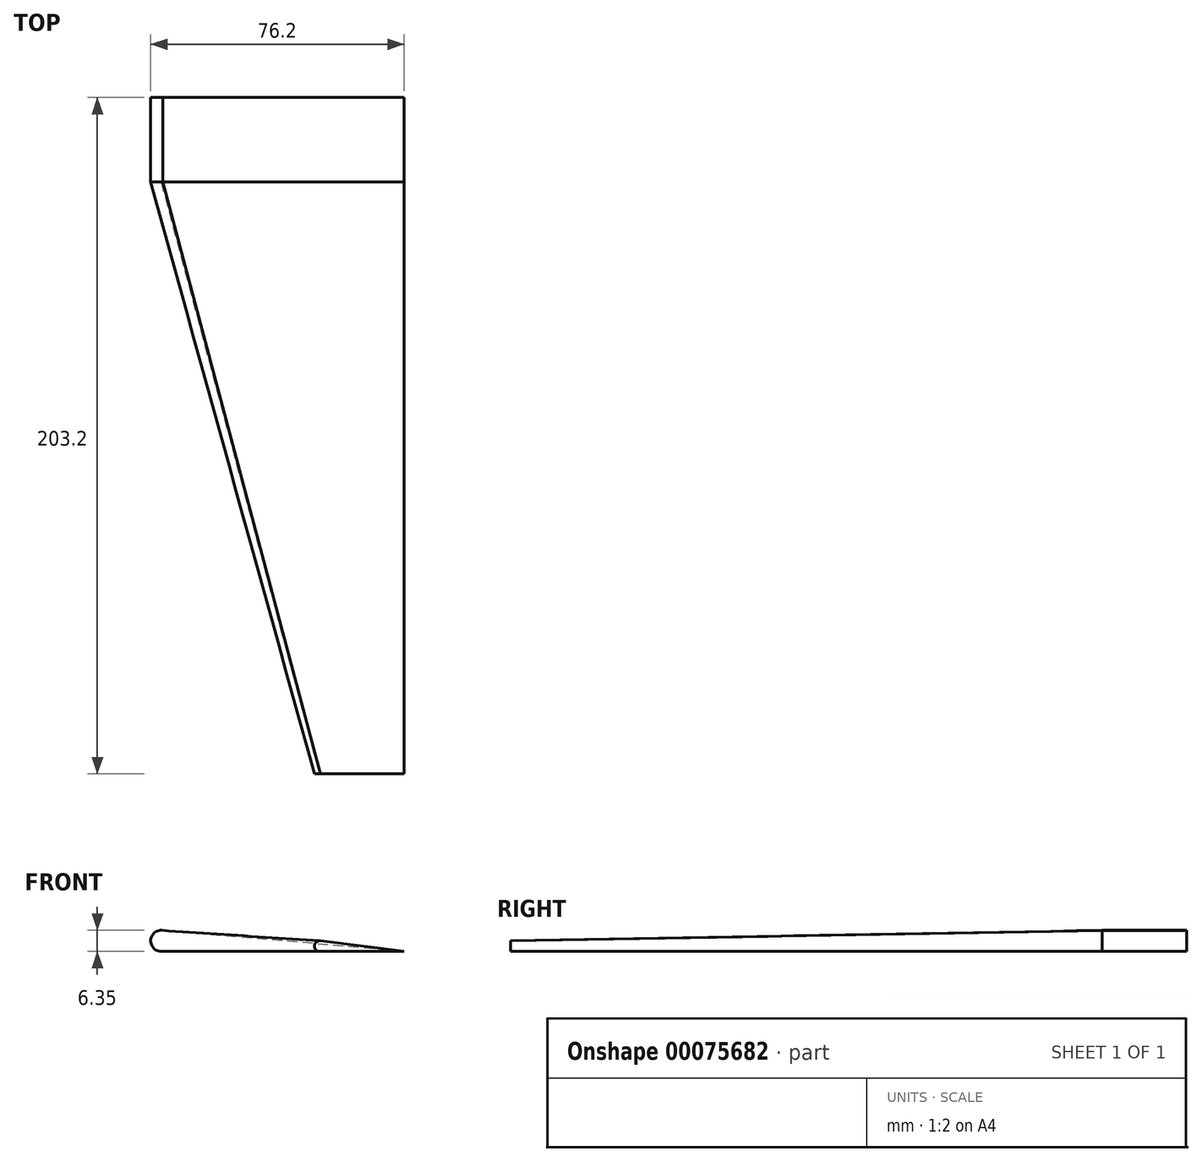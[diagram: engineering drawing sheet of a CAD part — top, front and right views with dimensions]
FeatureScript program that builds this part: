
annotation { "Feature Type Name" : "Feature", "Feature Type Description" : "" }
export const myFeature = defineFeature(function(context is Context, id is Id, definition is map)
    precondition{}
    {
        {
            var Q0;
            Q0=qCreatedBy(makeId("Front.planeOp"),FACE);
            var sketch = newSketch(context, id + "F0", { "sketchPlane" : qUnion([Q0])});
            skLineSegment(sketch, "E0", {"start": v(0, 0) * mm, "end": v(-72.58, 6.32) * mm});
            skLineSegment(sketch, "E1", {"start": v(0, 0) * mm, "end": v(-73.03, 0) * mm});
            skArc(sketch, "E2", {"start": v(-72.58, 6.32) * mm, "mid": v(-76.2, 3.4) * mm, "end": v(-73.03, 0) * mm});
            skSolve(sketch);
        }
        {
            var Q0;
            Q0=qCreatedBy(makeId("Front.planeOp"),FACE);
            cPlane(context, id + "F1", {"entities" : qUnion([Q0]), "cplaneType" : CPlaneType.OFFSET, "offset" : 203.2 * mm, "width" : 152.4 * mm, "height" : 152.4 * mm});
        }
        {
            var Q0;
            Q0=makeQuery(id+"F0.imprint","IMPRINT",FACE,{"disambiguationData":[TD([[makeQuery(id+"F0.imprint","IMPRINT",EDGE,{"derivedFrom":sQuery(id+"F0.wireOp",EDGE,"E0")}),1.0]])]});
            extrude(context, id + "F2", {"entities" : qUnion([Q0]), "depth" : 25.4 * mm});
        }
        {
            var Q0;
            Q0=qCreatedBy(id+"F1.planeOp",FACE);
            var sketch = newSketch(context, id + "F3", { "sketchPlane" : qUnion([Q0])});
            skPoint(sketch, "E3.0", {"position": v(0, 0) * mm});
            skLineSegment(sketch, "E4", {"start": v(0, 0) * mm, "end": v(-25.4, 0) * mm});
            skArc(sketch, "E5", {"start": v(-25.2, 3.16) * mm, "mid": v(-26.98, 1.69) * mm, "end": v(-25.4, 0) * mm});
            skLineSegment(sketch, "E6", {"start": v(0, 0) * mm, "end": v(-25.2, 3.16) * mm});
            skSolve(sketch);
        }
        {
            var Q1;
            Q1=makeQuery(id+"F2.opExtrude","CAP_FACE",FACE,{"disambiguationData":[OSD([sQuery(id+"F0.wireOp",EDGE,"E0"),sQuery(id+"F0.wireOp",EDGE,"E1"),sQuery(id+"F0.wireOp",EDGE,"E2")])],"isStart":false});
            var Q2;
            Q2=makeQuery(id+"F3.imprint","IMPRINT",FACE,{"disambiguationData":[TD([[makeQuery(id+"F3.imprint","IMPRINT",EDGE,{"derivedFrom":sQuery(id+"F3.wireOp",EDGE,"E4")}),-1.0]])]});
            loft(context, id + "F4", {"operationType" : NewBodyOperationType.ADD, "sheetProfilesArray" : [{ "sheetProfileEntities" : qUnion([Q1]) }, { "sheetProfileEntities" : qUnion([Q2]) }]});
        }
    });
